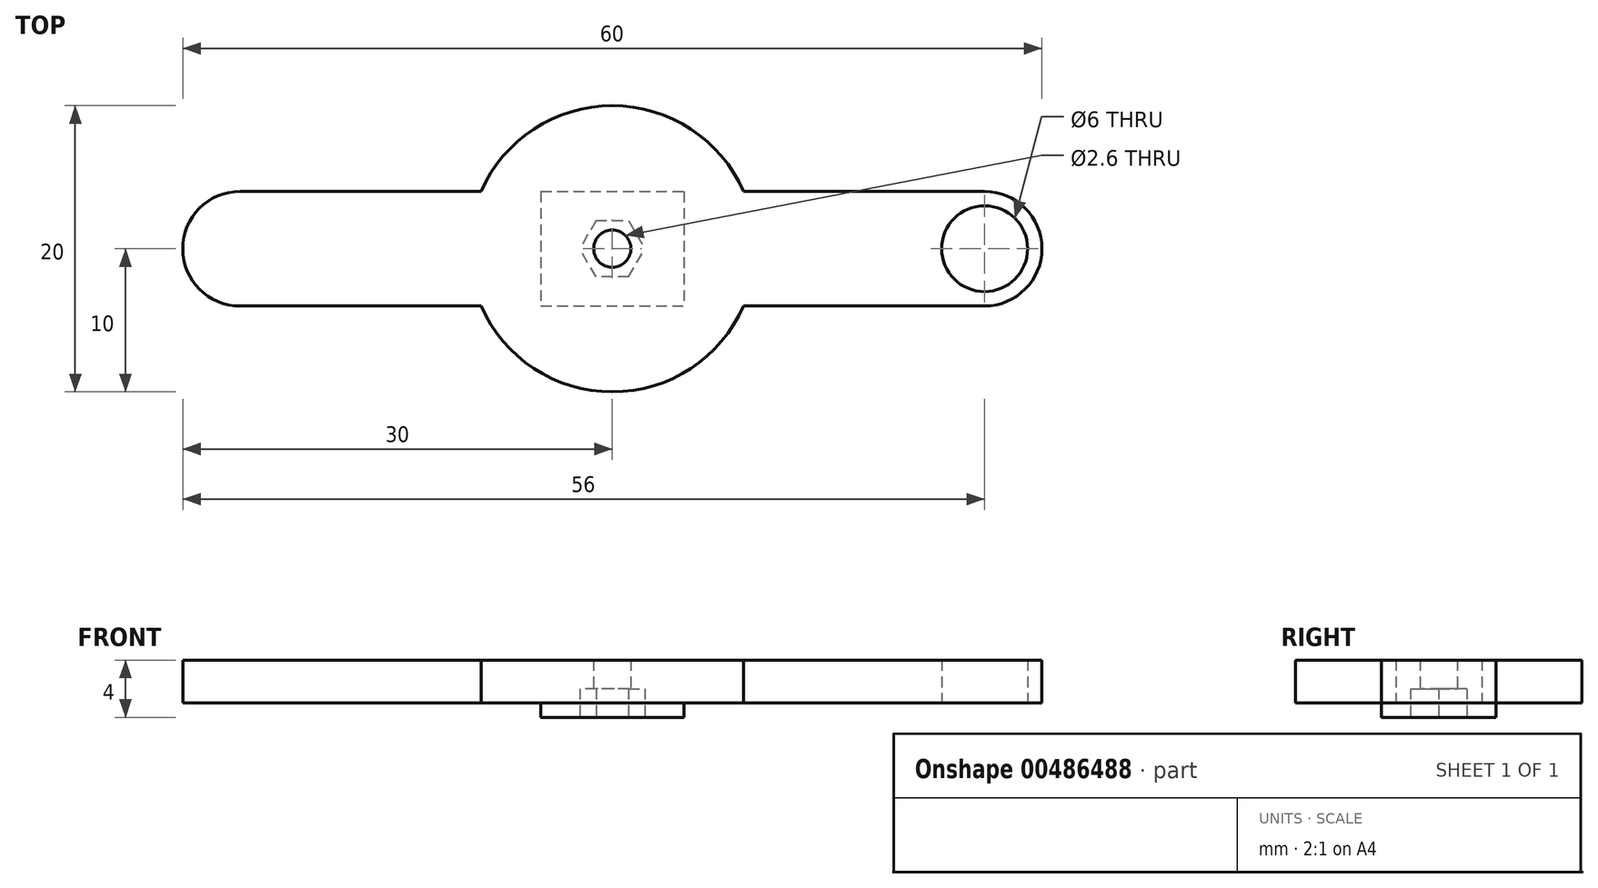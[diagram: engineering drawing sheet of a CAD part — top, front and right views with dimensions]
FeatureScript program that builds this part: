
annotation { "Feature Type Name" : "Feature", "Feature Type Description" : "" }
export const myFeature = defineFeature(function(context is Context, id is Id, definition is map)
    precondition{}
    {
        {
            var Q0;
            Q0=qCreatedBy(makeId("Top.planeOp"),FACE);
            var sketch = newSketch(context, id + "F0", { "sketchPlane" : qUnion([Q0])});
            skCircle(sketch, "E0", {"center": v(-26, 38) * mm, "radius": 1.7 * mm});
            skCircle(sketch, "E1.MirrorC", {"center": v(26, 38) * mm, "radius": 1.7 * mm});
            skCircle(sketch, "E2.MirrorC", {"center": v(-26, -38) * mm, "radius": 1.7 * mm});
            skCircle(sketch, "E3.MirrorC", {"center": v(26, -38) * mm, "radius": 1.7 * mm});
            skSolve(sketch);
        }
        {
            var Q0;
            Q0=qCreatedBy(makeId("Top.planeOp"),FACE);
            var sketch = newSketch(context, id + "F1", { "sketchPlane" : qUnion([Q0])});
            skCircle(sketch, "E4", {"center": v(-26, 38) * mm, "radius": 3 * mm});
            skCircle(sketch, "E5", {"center": v(-26, 38) * mm, "radius": 1.7 * mm});
            skCircle(sketch, "E6.MirrorC", {"center": v(26, 38) * mm, "radius": 1.7 * mm});
            skCircle(sketch, "E7.MirrorC", {"center": v(26, 38) * mm, "radius": 3 * mm});
            skLineSegment(sketch, "E8.bottom", {"start": v(-30, 42) * mm, "end": v(30, 42) * mm});
            skLineSegment(sketch, "E8.top", {"start": v(-30, 34) * mm, "end": v(30, 34) * mm});
            skLineSegment(sketch, "E8.left", {"start": v(-30, 42) * mm, "end": v(-30, 34) * mm});
            skLineSegment(sketch, "E8.right", {"start": v(30, 42) * mm, "end": v(30, 34) * mm});
            skSolve(sketch);
        }
        {
            var Q0;
            Q0=makeQuery(id+"F1.imprint","IMPRINT",FACE,{"disambiguationData":[TD([[makeQuery(id+"F1.imprint","IMPRINT",EDGE,{"derivedFrom":sQuery(id+"F1.wireOp",EDGE,"E4")}),-1.0]])]});
            var sketch = newSketch(context, id + "F2", { "sketchPlane" : qUnion([Q0])});
            skLineSegment(sketch, "E9", {"start": v(0, 38) * mm, "end": v(1.44, 35.5) * mm, "construction": true});
            skLineSegment(sketch, "E10", {"start": v(0, 38) * mm, "end": v(0, 36.02) * mm, "construction": true});
            skLineSegment(sketch, "E11", {"start": v(0, 36.02) * mm, "end": v(-1.14, 36.02) * mm});
            skLineSegment(sketch, "E12", {"start": v(-1.14, 36.02) * mm, "end": v(-2.28, 38) * mm});
            skLineSegment(sketch, "E13", {"start": v(-2.28, 38) * mm, "end": v(0, 38) * mm, "construction": true});
            skLineSegment(sketch, "E14.MirrorCS", {"start": v(-1.14, 39.97) * mm, "end": v(-2.28, 38) * mm});
            skLineSegment(sketch, "E15.MirrorCS", {"start": v(0, 39.97) * mm, "end": v(-1.14, 39.97) * mm});
            skLineSegment(sketch, "E16.MirrorCS", {"start": v(0, 36.02) * mm, "end": v(1.14, 36.02) * mm});
            skLineSegment(sketch, "E17.MirrorCS", {"start": v(1.14, 36.02) * mm, "end": v(2.28, 38) * mm});
            skLineSegment(sketch, "E18.MirrorCS", {"start": v(1.14, 39.97) * mm, "end": v(2.28, 38) * mm});
            skLineSegment(sketch, "E19.MirrorCS", {"start": v(0, 39.97) * mm, "end": v(1.14, 39.97) * mm});
            skSolve(sketch);
        }
        {
            var Q0;
            Q0=makeQuery(id+"F1.imprint","IMPRINT",FACE,{"disambiguationData":[TD([[makeQuery(id+"F1.imprint","IMPRINT",EDGE,{"derivedFrom":sQuery(id+"F1.wireOp",EDGE,"E4")}),-1.0]])]});
            var sketch = newSketch(context, id + "F3", { "sketchPlane" : qUnion([Q0])});
            skCircle(sketch, "E20", {"center": v(0, 38) * mm, "radius": 1.3 * mm});
            skSolve(sketch);
        }
        {
            var Q0;
            Q0=makeQuery(id+"F2.imprint","IMPRINT",FACE,{"disambiguationData":[TD([[makeQuery(id+"F2.imprint","IMPRINT",EDGE,{"derivedFrom":sQuery(id+"F2.wireOp",EDGE,"E11")}),1.0]])]});
            var Q1;
            Q1=makeQuery(id+"F2.imprint","IMPRINT",FACE,{"disambiguationData":[TD([[makeQuery(id+"F2.imprint","IMPRINT",EDGE,{"derivedFrom":sQuery(id+"F2.wireOp",EDGE,"E11")}),-1.0]])]});
            var Q2;
            Q2=makeQuery(id+"F2.imprint","IMPRINT",FACE,{"disambiguationData":[TD([[makeQuery(id+"F2.imprint","IMPRINT",EDGE,{"derivedFrom":makeQuery(id+"F1.imprint","IMPRINT",EDGE,{"derivedFrom":sQuery(id+"F1.wireOp",EDGE,"E4")})}),1.0]])]});
            var Q3;
            Q3=makeQuery(id+"F2.imprint","IMPRINT",FACE,{"disambiguationData":[TD([[makeQuery(id+"F2.imprint","IMPRINT",EDGE,{"derivedFrom":makeQuery(id+"F1.imprint","IMPRINT",EDGE,{"derivedFrom":sQuery(id+"F1.wireOp",EDGE,"E7.MirrorC")})}),-1.0]])]});
            extrude(context, id + "F4", {"entities" : qUnion([Q0, Q1, Q2, Q3]), "depth" : 4 * mm, "offsetDistance" : 25 * mm});
        }
        {
            var Q0;
            Q0=makeQuery(id+"F4.opExtrude","SWEPT_EDGE",EDGE,{"disambiguationData":[OSD([sQuery(id+"F1.wireOp",EDGE,"E8.bottom"),sQuery(id+"F1.wireOp",EDGE,"E8.left")])]});
            var Q1;
            Q1=makeQuery(id+"F4.opExtrude","SWEPT_EDGE",EDGE,{"disambiguationData":[OSD([sQuery(id+"F1.wireOp",EDGE,"E8.top"),sQuery(id+"F1.wireOp",EDGE,"E8.left")])]});
            var Q2;
            Q2=makeQuery(id+"F4.opExtrude","SWEPT_EDGE",EDGE,{"disambiguationData":[OSD([sQuery(id+"F1.wireOp",EDGE,"E8.bottom"),sQuery(id+"F1.wireOp",EDGE,"E8.right")])]});
            var Q3;
            Q3=makeQuery(id+"F4.opExtrude","SWEPT_EDGE",EDGE,{"disambiguationData":[OSD([sQuery(id+"F1.wireOp",EDGE,"E8.top"),sQuery(id+"F1.wireOp",EDGE,"E8.right")])]});
            fillet(context, id + "F5", {"entities" : qUnion([Q0, Q1, Q2, Q3]), "radius" : 4 * mm, "tangentPropagation" : true, "allowEdgeOverflow" : false});
        }
        {
            var Q0;
            Q0=makeQuery(id+"F4.opExtrude","CAP_FACE",FACE,{"disambiguationData":[OSD([sQuery(id+"F1.wireOp",EDGE,"E8.bottom"),sQuery(id+"F1.wireOp",EDGE,"E8.top"),sQuery(id+"F1.wireOp",EDGE,"E8.left"),sQuery(id+"F1.wireOp",EDGE,"E8.right")])],"isStart":false});
            var sketch = newSketch(context, id + "F6", { "sketchPlane" : qUnion([Q0])});
            skCircle(sketch, "E21", {"center": v(0, 38) * mm, "radius": 10 * mm});
            skSolve(sketch);
        }
        {
            var Q0;
            Q0 = qSketchRegion(id + "F6", true);
            extrude(context, id + "F7", {"entities" : qUnion([Q0]), "operationType" : NewBodyOperationType.ADD, "oppositeDirection" : true, "depth" : 3 * mm, "offsetDistance" : 25 * mm});
        }
        {
            var Q0;
            Q0=qSketchRegion(id+"F3",true);
            extrude(context, id + "F8", {"entities" : qUnion([Q0]), "operationType" : NewBodyOperationType.REMOVE, "endBound" : BoundingType.THROUGH_ALL, "depth" : 25 * mm, "offsetDistance" : 25 * mm});
        }
        {
            var Q0;
            Q0=makeQuery(id+"F1.imprint","IMPRINT",FACE,{"disambiguationData":[TD([[makeQuery(id+"F1.imprint","IMPRINT",EDGE,{"derivedFrom":sQuery(id+"F1.wireOp",EDGE,"E4")}),-1.0]])]});
            var sketch = newSketch(context, id + "F9", { "sketchPlane" : qUnion([Q0])});
            skLineSegment(sketch, "E22.bottom", {"start": v(30, 42) * mm, "end": v(5, 42) * mm});
            skLineSegment(sketch, "E22.top", {"start": v(30, 34) * mm, "end": v(5, 34) * mm});
            skLineSegment(sketch, "E22.left", {"start": v(30, 42) * mm, "end": v(30, 34) * mm});
            skLineSegment(sketch, "E22.right", {"start": v(5, 42) * mm, "end": v(5, 34) * mm});
            skLineSegment(sketch, "E23.MirrorCS", {"start": v(-5, 42) * mm, "end": v(-5, 34) * mm});
            skLineSegment(sketch, "E24.MirrorCS", {"start": v(-30, 34) * mm, "end": v(-5, 34) * mm});
            skLineSegment(sketch, "E25.MirrorCS", {"start": v(-30, 42) * mm, "end": v(-5, 42) * mm});
            skLineSegment(sketch, "E26.MirrorCS", {"start": v(-30, 42) * mm, "end": v(-30, 34) * mm});
            skSolve(sketch);
        }
        {
            var Q0;
            Q0 = qSketchRegion(id + "F9", true);
            extrude(context, id + "F10", {"entities" : qUnion([Q0]), "operationType" : NewBodyOperationType.REMOVE, "depth" : 1 * mm, "offsetDistance" : 25 * mm});
        }
        {
            var Q0;
            Q0=qSketchRegion(id+"F2",true);
            extrude(context, id + "F11", {"entities" : qUnion([Q0]), "operationType" : NewBodyOperationType.REMOVE, "depth" : 2 * mm, "offsetDistance" : 25 * mm});
        }
    });
